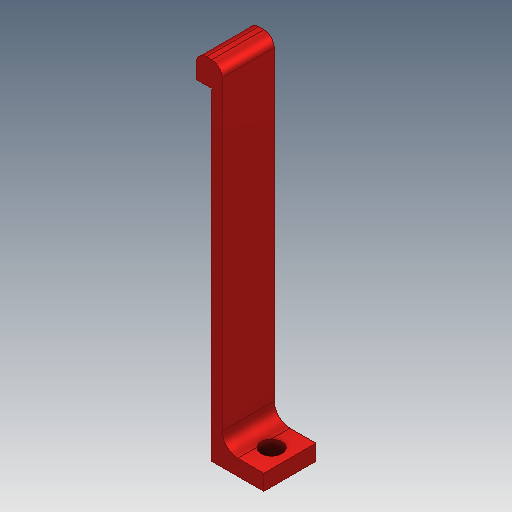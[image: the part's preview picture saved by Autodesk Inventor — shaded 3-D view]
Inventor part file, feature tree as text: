
AUTODESK INVENTOR PART (.ipt)
format: ipt  version: 2020 (Build 240168000, 168)  size: 138,240 bytes
history: native  units: in
note: dims shown in document units (in); Inventor stores cm internally (conversion verified against a paired STEP export)
features: extrude x4, sketch x3, fillet x2
ambient origin geometry x8: Origin, YZ Plane, XZ Plane, XY Plane, X Axis, Y Axis, Z Axis, Center Point
bodies: Solid1 (feature_tree)
feature tree (9):
  sketch  "Sketch1"  dims[d0=0.3937in d1=0.3937in]
  extrude  "Extrusion1"  Depth=0.3937in
  extrude  "Extrusion2"  Depth=0.1181in TaperAngle=0.0deg
  extrude  "Extrusion3"  Depth=0.0787in
  fillet  "Fillet1"  Radius=0.1575in
  extrude  "Extrusion4"  Depth=2.4409in TaperAngle=0.0deg
  fillet  "Fillet2"  Radius=0.1181in
  sketch  "Sketch2"  dims[d2=0.0787in d3=0.1181in d4=0.0in]
  sketch  "Sketch3"  dims[d5=2.4409in d6=0.0in d7=0.1378in d8=0.1575in d9=2.4409in d10=0.0in d11=0.1181in d12=0.1181in d13=0.0787in d14=0.0in d15=0.0in d16=0.0787in]
